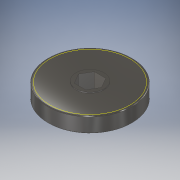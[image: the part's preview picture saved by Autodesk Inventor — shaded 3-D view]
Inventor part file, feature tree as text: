
AUTODESK INVENTOR PART (.ipt)
format: ipt  version: 2018 (Build 220112000, 112)  size: 143,360 bytes
history: native  units: in
note: dims shown in document units (in); Inventor stores cm internally (conversion verified against a paired STEP export)
features: other x3, sketch x1
ambient origin geometry x8: Origin, YZ Plane, XZ Plane, XY Plane, X Axis, Y Axis, Z Axis, Center Point
bodies: Solid1 (feature_tree)
feature tree (4):
  sketch  "Sketch1"  dims[d0=2.0in d1=1.0in d2=0.0in]
  other  "Srf1"
  other  "Cut-Extrude2"
  other  "pitch circle"
